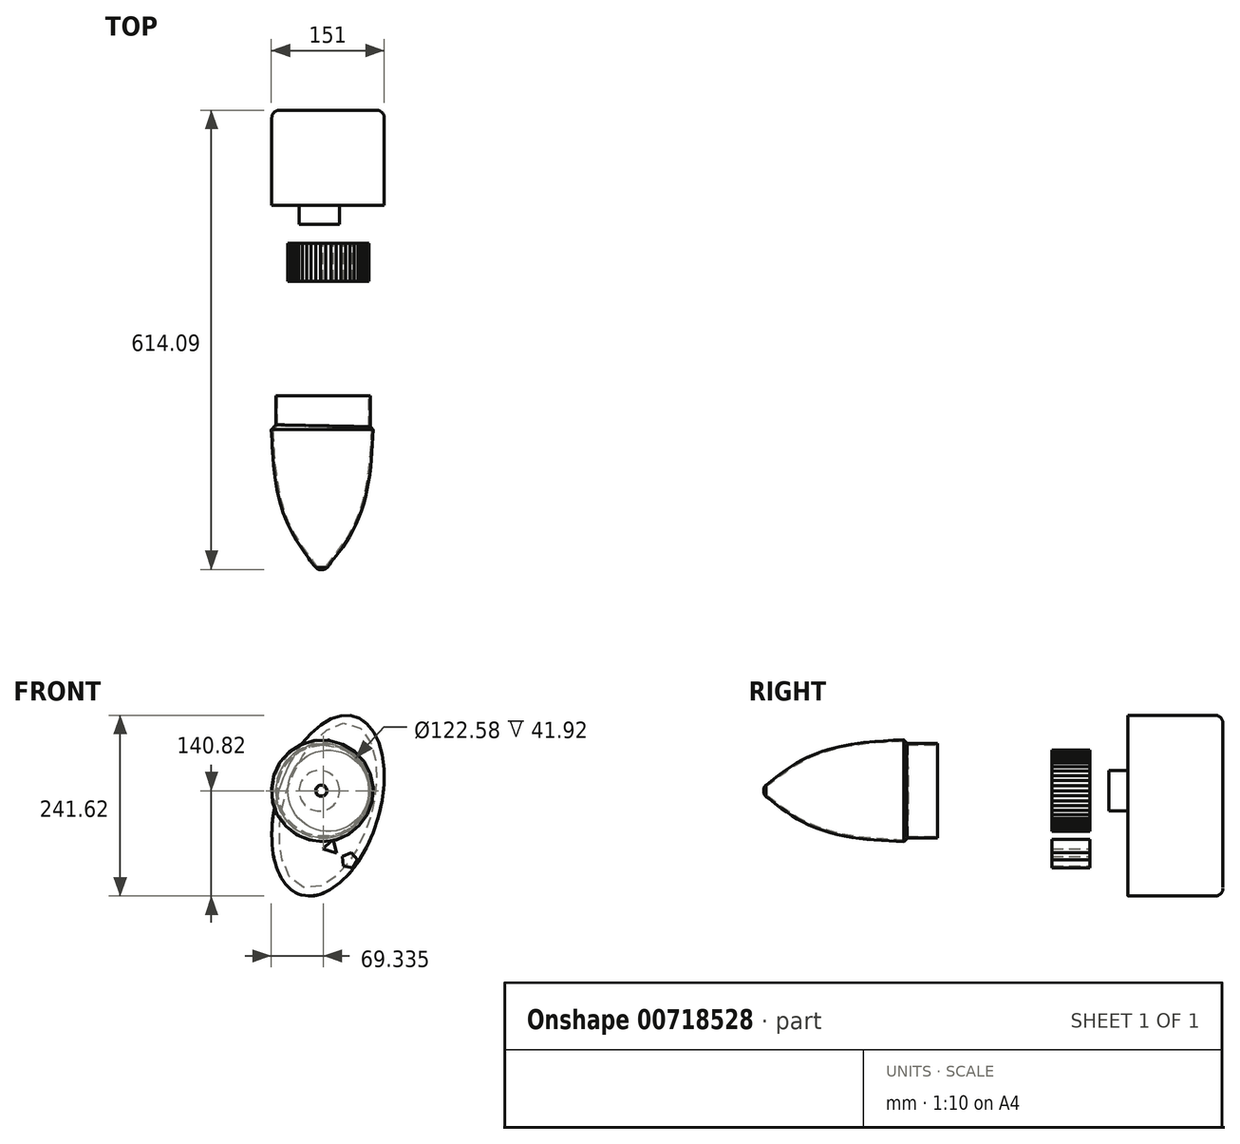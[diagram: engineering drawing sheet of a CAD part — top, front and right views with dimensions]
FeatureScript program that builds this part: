
annotation { "Feature Type Name" : "Feature", "Feature Type Description" : "" }
export const myFeature = defineFeature(function(context is Context, id is Id, definition is map)
    precondition{}
    {
        {
            var Q0;
            Q0=qCreatedBy(makeId("Front.planeOp"),FACE);
            var sketch = newSketch(context, id + "F0", { "sketchPlane" : qUnion([Q0])});
            skEllipse(sketch, "E0", {"center": v(65.97, -20) * mm, "majorRadius": 68.93 * mm, "minorRadius": 124.5 * mm, "majorAxis": v(-0.96, 0.3)});
            skSolve(sketch);
        }
        {
            var Q0;
            Q0=makeQuery(id+"F0.imprint","IMPRINT",FACE,{"disambiguationData":[TD([[makeQuery(id+"F0.imprint","IMPRINT",EDGE,{"derivedFrom":sQuery(id+"F0.wireOp",EDGE,"E0")}),1.0]])]});
            extrude(context, id + "F1", {"entities" : qUnion([Q0]), "depth" : 127 * mm, "offsetDistance" : 25.4 * mm});
        }
        {
            var Q0;
            Q0=makeQuery(id+"F1.opExtrude","CAP_EDGE",EDGE,{"disambiguationData":[OSD([sQuery(id+"F0.wireOp",EDGE,"E0")])],"isStart":true});
            fillet(context, id + "F2", {"entities" : qUnion([Q0]), "radius" : 10.16 * mm, "tangentPropagation" : true, "allowEdgeOverflow" : false});
        }
        {
            var Q0;
            Q0=makeQuery(id+"F1.opExtrude","CAP_FACE",FACE,{"disambiguationData":[OSD([sQuery(id+"F0.wireOp",EDGE,"E0")])],"isStart":false});
            var sketch = newSketch(context, id + "F3", { "sketchPlane" : qUnion([Q0])});
            skCircle(sketch, "E1", {"center": v(54.3, 0) * mm, "radius": 27.07 * mm});
            skSolve(sketch);
        }
        {
            var Q0;
            Q0 = qSketchRegion(id + "F3", true);
            extrude(context, id + "F4", {"entities" : qUnion([Q0]), "operationType" : NewBodyOperationType.ADD, "depth" : 25.4 * mm, "offsetDistance" : 25.4 * mm});
        }
        {
            var Q0;
            Q0=makeQuery(id+"F1.opExtrude","CAP_FACE",FACE,{"disambiguationData":[OSD([sQuery(id+"F0.wireOp",EDGE,"E0")])],"isStart":false});
            cPlane(context, id + "F5", {"entities" : qUnion([Q0]), "cplaneType" : CPlaneType.OFFSET, "offset" : 50.8 * mm, "width" : 152.4 * mm, "height" : 152.4 * mm});
        }
        {
            var Q0;
            Q0=qCreatedBy(id+"F5.planeOp",FACE);
            var sketch = newSketch(context, id + "F6", { "sketchPlane" : qUnion([Q0])});
            skCircle(sketch, "E2.cCircle", {"center": v(-818.72, 4123.6) * mm, "radius": 253.69 * mm, "construction": true});
            skLineSegment(sketch, "E2.0", {"start": v(-616.57, 3970.34) * mm, "end": v(-850.38, 3871.9) * mm});
            skLineSegment(sketch, "E2.1", {"start": v(-850.38, 3871.9) * mm, "end": v(-1052.53, 4025.17) * mm});
            skLineSegment(sketch, "E2.2", {"start": v(-1052.53, 4025.17) * mm, "end": v(-1020.87, 4276.87) * mm});
            skLineSegment(sketch, "E2.3", {"start": v(-1020.87, 4276.87) * mm, "end": v(-787.06, 4375.3) * mm});
            skLineSegment(sketch, "E2.4", {"start": v(-787.06, 4375.3) * mm, "end": v(-584.91, 4222.04) * mm});
            skLineSegment(sketch, "E2.5", {"start": v(-584.91, 4222.04) * mm, "end": v(-616.57, 3970.34) * mm});
            skCircle(sketch, "E3.cCircle", {"center": v(66.43, 0) * mm, "radius": 54.26 * mm, "construction": true});
            skLineSegment(sketch, "E3.0", {"start": v(120.7, 0) * mm, "end": v(120.27, -6.8) * mm});
            skLineSegment(sketch, "E3.1", {"start": v(120.27, -6.8) * mm, "end": v(119, -13.5) * mm});
            skLineSegment(sketch, "E3.2", {"start": v(119, -13.5) * mm, "end": v(116.89, -19.98) * mm});
            skLineSegment(sketch, "E3.3", {"start": v(116.89, -19.98) * mm, "end": v(113.99, -26.14) * mm});
            skLineSegment(sketch, "E3.4", {"start": v(113.99, -26.14) * mm, "end": v(110.33, -31.9) * mm});
            skLineSegment(sketch, "E3.5", {"start": v(110.33, -31.9) * mm, "end": v(106, -37.15) * mm});
            skLineSegment(sketch, "E3.6", {"start": v(106, -37.15) * mm, "end": v(101.02, -41.81) * mm});
            skLineSegment(sketch, "E3.7", {"start": v(101.02, -41.81) * mm, "end": v(95.51, -45.82) * mm});
            skLineSegment(sketch, "E3.8", {"start": v(95.51, -45.82) * mm, "end": v(89.54, -49.1) * mm});
            skLineSegment(sketch, "E3.9", {"start": v(89.54, -49.1) * mm, "end": v(83.2, -51.6) * mm});
            skLineSegment(sketch, "E3.10", {"start": v(83.2, -51.6) * mm, "end": v(76.6, -53.3) * mm});
            skLineSegment(sketch, "E3.11", {"start": v(76.6, -53.3) * mm, "end": v(69.84, -54.16) * mm});
            skLineSegment(sketch, "E3.12", {"start": v(69.84, -54.16) * mm, "end": v(63.03, -54.16) * mm});
            skLineSegment(sketch, "E3.13", {"start": v(63.03, -54.16) * mm, "end": v(56.27, -53.3) * mm});
            skLineSegment(sketch, "E3.14", {"start": v(56.27, -53.3) * mm, "end": v(49.67, -51.6) * mm});
            skLineSegment(sketch, "E3.15", {"start": v(49.67, -51.6) * mm, "end": v(43.33, -49.1) * mm});
            skLineSegment(sketch, "E3.16", {"start": v(43.33, -49.1) * mm, "end": v(37.36, -45.82) * mm});
            skLineSegment(sketch, "E3.17", {"start": v(37.36, -45.82) * mm, "end": v(31.84, -41.81) * mm});
            skLineSegment(sketch, "E3.18", {"start": v(31.84, -41.81) * mm, "end": v(26.88, -37.15) * mm});
            skLineSegment(sketch, "E3.19", {"start": v(26.88, -37.15) * mm, "end": v(22.53, -31.9) * mm});
            skLineSegment(sketch, "E3.20", {"start": v(22.53, -31.9) * mm, "end": v(18.88, -26.14) * mm});
            skLineSegment(sketch, "E3.21", {"start": v(18.88, -26.14) * mm, "end": v(15.98, -19.98) * mm});
            skLineSegment(sketch, "E3.22", {"start": v(15.98, -19.98) * mm, "end": v(13.87, -13.5) * mm});
            skLineSegment(sketch, "E3.23", {"start": v(13.87, -13.5) * mm, "end": v(12.6, -6.8) * mm});
            skLineSegment(sketch, "E3.24", {"start": v(12.6, -6.8) * mm, "end": v(12.17, 0) * mm});
            skLineSegment(sketch, "E3.25", {"start": v(12.17, 0) * mm, "end": v(12.6, 6.8) * mm});
            skLineSegment(sketch, "E3.26", {"start": v(12.6, 6.8) * mm, "end": v(13.87, 13.5) * mm});
            skLineSegment(sketch, "E3.27", {"start": v(13.87, 13.5) * mm, "end": v(15.98, 19.98) * mm});
            skLineSegment(sketch, "E3.28", {"start": v(15.98, 19.98) * mm, "end": v(18.88, 26.14) * mm});
            skLineSegment(sketch, "E3.29", {"start": v(18.88, 26.14) * mm, "end": v(22.53, 31.9) * mm});
            skLineSegment(sketch, "E3.30", {"start": v(22.53, 31.9) * mm, "end": v(26.88, 37.15) * mm});
            skLineSegment(sketch, "E3.31", {"start": v(26.88, 37.15) * mm, "end": v(31.84, 41.81) * mm});
            skLineSegment(sketch, "E3.32", {"start": v(31.84, 41.81) * mm, "end": v(37.36, 45.82) * mm});
            skLineSegment(sketch, "E3.33", {"start": v(37.36, 45.82) * mm, "end": v(43.33, 49.1) * mm});
            skLineSegment(sketch, "E3.34", {"start": v(43.33, 49.1) * mm, "end": v(49.67, 51.6) * mm});
            skLineSegment(sketch, "E3.35", {"start": v(49.67, 51.6) * mm, "end": v(56.27, 53.3) * mm});
            skLineSegment(sketch, "E3.36", {"start": v(56.27, 53.3) * mm, "end": v(63.03, 54.16) * mm});
            skLineSegment(sketch, "E3.37", {"start": v(63.03, 54.16) * mm, "end": v(69.84, 54.16) * mm});
            skLineSegment(sketch, "E3.38", {"start": v(69.84, 54.16) * mm, "end": v(76.6, 53.3) * mm});
            skLineSegment(sketch, "E3.39", {"start": v(76.6, 53.3) * mm, "end": v(83.2, 51.6) * mm});
            skLineSegment(sketch, "E3.40", {"start": v(83.2, 51.6) * mm, "end": v(89.54, 49.1) * mm});
            skLineSegment(sketch, "E3.41", {"start": v(89.54, 49.1) * mm, "end": v(95.51, 45.82) * mm});
            skLineSegment(sketch, "E3.42", {"start": v(95.51, 45.82) * mm, "end": v(101.02, 41.81) * mm});
            skLineSegment(sketch, "E3.43", {"start": v(101.02, 41.81) * mm, "end": v(106, 37.15) * mm});
            skLineSegment(sketch, "E3.44", {"start": v(106, 37.15) * mm, "end": v(110.33, 31.9) * mm});
            skLineSegment(sketch, "E3.45", {"start": v(110.33, 31.9) * mm, "end": v(113.99, 26.14) * mm});
            skLineSegment(sketch, "E3.46", {"start": v(113.99, 26.14) * mm, "end": v(116.89, 19.98) * mm});
            skLineSegment(sketch, "E3.47", {"start": v(116.89, 19.98) * mm, "end": v(119, 13.5) * mm});
            skLineSegment(sketch, "E3.48", {"start": v(119, 13.5) * mm, "end": v(120.27, 6.8) * mm});
            skLineSegment(sketch, "E3.49", {"start": v(120.27, 6.8) * mm, "end": v(120.7, 0) * mm});
            skCircle(sketch, "E4.cCircle", {"center": v(69.84, -75.35) * mm, "radius": 11 * mm, "construction": true});
            skLineSegment(sketch, "E4.0", {"start": v(77.49, -83.26) * mm, "end": v(59.16, -78.01) * mm});
            skLineSegment(sketch, "E4.1", {"start": v(59.16, -78.01) * mm, "end": v(72.87, -64.77) * mm});
            skLineSegment(sketch, "E4.2", {"start": v(72.87, -64.77) * mm, "end": v(77.49, -83.26) * mm});
            skCircle(sketch, "E5.cCircle", {"center": v(94.71, -93.16) * mm, "radius": 10.8 * mm, "construction": true});
            skLineSegment(sketch, "E5.0", {"start": v(99.01, -103.06) * mm, "end": v(86.63, -100.3) * mm});
            skLineSegment(sketch, "E5.1", {"start": v(86.63, -100.3) * mm, "end": v(85.42, -87.68) * mm});
            skLineSegment(sketch, "E5.2", {"start": v(85.42, -87.68) * mm, "end": v(97.05, -82.63) * mm});
            skLineSegment(sketch, "E5.3", {"start": v(97.05, -82.63) * mm, "end": v(105.46, -92.13) * mm});
            skLineSegment(sketch, "E5.4", {"start": v(105.46, -92.13) * mm, "end": v(99.01, -103.06) * mm});
            skSolve(sketch);
        }
        {
            var Q0;
            Q0=makeQuery(id+"F6.imprint","IMPRINT",FACE,{"disambiguationData":[TD([[makeQuery(id+"F6.imprint","IMPRINT",EDGE,{"derivedFrom":sQuery(id+"F6.wireOp",EDGE,"E3.0")}),-1.0]])]});
            var Q1;
            Q1=makeQuery(id+"F6.imprint","IMPRINT",FACE,{"disambiguationData":[TD([[makeQuery(id+"F6.imprint","IMPRINT",EDGE,{"derivedFrom":sQuery(id+"F6.wireOp",EDGE,"E5.0")}),-1.0]])]});
            var Q2;
            Q2=makeQuery(id+"F6.imprint","IMPRINT",FACE,{"disambiguationData":[TD([[makeQuery(id+"F6.imprint","IMPRINT",EDGE,{"derivedFrom":sQuery(id+"F6.wireOp",EDGE,"E4.0")}),-1.0]])]});
            extrude(context, id + "F7", {"entities" : qUnion([Q0, Q1, Q2]), "depth" : 50.8 * mm, "offsetDistance" : 25.4 * mm});
        }
        {
            var Q0;
            Q0=makeQuery(id+"F7.opExtrude","CAP_FACE",FACE,{"disambiguationData":[OSD([sQuery(id+"F6.wireOp",EDGE,"E3.0"),sQuery(id+"F6.wireOp",EDGE,"E3.1"),sQuery(id+"F6.wireOp",EDGE,"E3.2"),sQuery(id+"F6.wireOp",EDGE,"E3.3"),sQuery(id+"F6.wireOp",EDGE,"E3.4"),sQuery(id+"F6.wireOp",EDGE,"E3.5"),sQuery(id+"F6.wireOp",EDGE,"E3.6"),sQuery(id+"F6.wireOp",EDGE,"E3.7"),sQuery(id+"F6.wireOp",EDGE,"E3.8"),sQuery(id+"F6.wireOp",EDGE,"E3.9"),sQuery(id+"F6.wireOp",EDGE,"E3.10"),sQuery(id+"F6.wireOp",EDGE,"E3.11"),sQuery(id+"F6.wireOp",EDGE,"E3.12"),sQuery(id+"F6.wireOp",EDGE,"E3.13"),sQuery(id+"F6.wireOp",EDGE,"E3.14"),sQuery(id+"F6.wireOp",EDGE,"E3.15"),sQuery(id+"F6.wireOp",EDGE,"E3.16"),sQuery(id+"F6.wireOp",EDGE,"E3.17"),sQuery(id+"F6.wireOp",EDGE,"E3.18"),sQuery(id+"F6.wireOp",EDGE,"E3.19"),sQuery(id+"F6.wireOp",EDGE,"E3.20"),sQuery(id+"F6.wireOp",EDGE,"E3.21"),sQuery(id+"F6.wireOp",EDGE,"E3.22"),sQuery(id+"F6.wireOp",EDGE,"E3.23"),sQuery(id+"F6.wireOp",EDGE,"E3.24"),sQuery(id+"F6.wireOp",EDGE,"E3.25"),sQuery(id+"F6.wireOp",EDGE,"E3.26"),sQuery(id+"F6.wireOp",EDGE,"E3.27"),sQuery(id+"F6.wireOp",EDGE,"E3.28"),sQuery(id+"F6.wireOp",EDGE,"E3.29"),sQuery(id+"F6.wireOp",EDGE,"E3.30"),sQuery(id+"F6.wireOp",EDGE,"E3.31"),sQuery(id+"F6.wireOp",EDGE,"E3.32"),sQuery(id+"F6.wireOp",EDGE,"E3.33"),sQuery(id+"F6.wireOp",EDGE,"E3.34"),sQuery(id+"F6.wireOp",EDGE,"E3.35"),sQuery(id+"F6.wireOp",EDGE,"E3.36"),sQuery(id+"F6.wireOp",EDGE,"E3.37"),sQuery(id+"F6.wireOp",EDGE,"E3.38"),sQuery(id+"F6.wireOp",EDGE,"E3.39"),sQuery(id+"F6.wireOp",EDGE,"E3.40"),sQuery(id+"F6.wireOp",EDGE,"E3.41"),sQuery(id+"F6.wireOp",EDGE,"E3.42"),sQuery(id+"F6.wireOp",EDGE,"E3.43"),sQuery(id+"F6.wireOp",EDGE,"E3.44"),sQuery(id+"F6.wireOp",EDGE,"E3.45"),sQuery(id+"F6.wireOp",EDGE,"E3.46"),sQuery(id+"F6.wireOp",EDGE,"E3.47"),sQuery(id+"F6.wireOp",EDGE,"E3.48"),sQuery(id+"F6.wireOp",EDGE,"E3.49")])],"isStart":false});
            cPlane(context, id + "F8", {"entities" : qUnion([Q0]), "cplaneType" : CPlaneType.OFFSET, "offset" : 103.5 * mm, "width" : 150 * mm, "height" : 150 * mm});
        }
        {
            var Q0;
            Q0=qCreatedBy(id+"F8.planeOp",FACE);
            var sketch = newSketch(context, id + "F9", { "sketchPlane" : qUnion([Q0])});
            skCircle(sketch, "E6", {"center": v(59.42, 0) * mm, "radius": 59.03 * mm});
            skSolve(sketch);
        }
        {
            var Q0;
            Q0=makeQuery(id+"F9.imprint","IMPRINT",FACE,{"disambiguationData":[TD([[makeQuery(id+"F9.imprint","IMPRINT",EDGE,{"derivedFrom":sQuery(id+"F9.wireOp",EDGE,"E6")}),1.0]])]});
            cPlane(context, id + "F10", {"entities" : qUnion([Q0]), "cplaneType" : CPlaneType.OFFSET, "offset" : 50 * mm, "width" : 150 * mm, "height" : 150 * mm});
        }
        {
            var Q0;
            Q0=qCreatedBy(id+"F10.planeOp",FACE);
            var sketch = newSketch(context, id + "F11", { "sketchPlane" : qUnion([Q0])});
            skCircle(sketch, "E7", {"center": v(59.52, 0) * mm, "radius": 61.29 * mm});
            skSolve(sketch);
        }
        {
            var Q0;
            Q0=makeQuery(id+"F11.imprint","IMPRINT",FACE,{"disambiguationData":[TD([[makeQuery(id+"F11.imprint","IMPRINT",EDGE,{"derivedFrom":sQuery(id+"F11.wireOp",EDGE,"E7")}),1.0]])]});
            cPlane(context, id + "F12", {"entities" : qUnion([Q0]), "cplaneType" : CPlaneType.OFFSET, "offset" : 30 * mm, "width" : 150 * mm, "height" : 150 * mm});
        }
        {
            var Q0;
            Q0=qCreatedBy(id+"F12.planeOp",FACE);
            var sketch = newSketch(context, id + "F13", { "sketchPlane" : qUnion([Q0])});
            skCircle(sketch, "E8", {"center": v(58.32, 0) * mm, "radius": 66.66 * mm});
            skSolve(sketch);
        }
        {
            var Q0;
            Q0=makeQuery(id+"F13.imprint","IMPRINT",FACE,{"disambiguationData":[TD([[makeQuery(id+"F13.imprint","IMPRINT",EDGE,{"derivedFrom":sQuery(id+"F13.wireOp",EDGE,"E8")}),1.0]])]});
            cPlane(context, id + "F14", {"entities" : qUnion([Q0]), "cplaneType" : CPlaneType.OFFSET, "offset" : 200 * mm, "width" : 150 * mm, "height" : 150 * mm});
        }
        {
            var Q0;
            Q0=qCreatedBy(id+"F14.planeOp",FACE);
            var sketch = newSketch(context, id + "F15", { "sketchPlane" : qUnion([Q0])});
            skCircle(sketch, "E9", {"center": v(57.1, 0) * mm, "radius": 4.48 * mm});
            skSolve(sketch);
        }
        {
            var Q0;
            Q0=sQuery(id+"F9.wireOp",EDGE,"E6");
            extrude(context, id + "F16", {"bodyType" : ToolBodyType.SURFACE, "surfaceEntities" : qUnion([Q0]), "depth" : 50 * mm, "offsetDistance" : 25 * mm});
        }
        {
            var Q0;
            Q0=makeQuery(id+"F11.imprint","IMPRINT",FACE,{"disambiguationData":[TD([[makeQuery(id+"F11.imprint","IMPRINT",EDGE,{"derivedFrom":sQuery(id+"F11.wireOp",EDGE,"E7")}),1.0]])]});
            extrude(context, id + "F17", {"entities" : qUnion([Q0]), "depth" : 30 * mm, "offsetDistance" : 25 * mm});
        }
        {
            var Q0;
            Q0=makeQuery(id+"F13.imprint","IMPRINT",FACE,{"disambiguationData":[TD([[makeQuery(id+"F13.imprint","IMPRINT",EDGE,{"derivedFrom":sQuery(id+"F13.wireOp",EDGE,"E8")}),1.0]])]});
            cPlane(context, id + "F18", {"entities" : qUnion([Q0]), "cplaneType" : CPlaneType.OFFSET, "offset" : 50 * mm, "width" : 150 * mm, "height" : 150 * mm});
        }
        {
            var Q0;
            Q0=qCreatedBy(id+"F18.planeOp",FACE);
            cPlane(context, id + "F19", {"entities" : qUnion([Q0]), "cplaneType" : CPlaneType.OFFSET, "offset" : 100 * mm, "width" : 150 * mm, "height" : 150 * mm});
        }
        {
            var Q0;
            Q0=qCreatedBy(id+"F19.planeOp",FACE);
            var sketch = newSketch(context, id + "F20", { "sketchPlane" : qUnion([Q0])});
            skCircle(sketch, "E10", {"center": v(57.7, 0) * mm, "radius": 39.32 * mm});
            skSolve(sketch);
        }
        {
            var Q1;
            Q1 = qSketchRegion(id + "F15", true);
            var Q2;
            Q2 = qSketchRegion(id + "F20", true);
            var Q3;
            Q3 = qSketchRegion(id + "F13", true);
            loft(context, id + "F21", {"operationType" : NewBodyOperationType.ADD, "sheetProfilesArray" : [{ "sheetProfileEntities" : qUnion([Q1]) }, { "sheetProfileEntities" : qUnion([Q2]) }, { "sheetProfileEntities" : qUnion([Q3]) }]});
        }
        {
            var Q0;
            Q0=makeQuery(id+"F21.opLoft","MID_CAP_EDGE",EDGE,{"disambiguationData":[OSD([sQuery(id+"F15.wireOp",EDGE,"E9")])],"capPos":0.0});
            fillet(context, id + "F22", {"entities" : qUnion([Q0]), "radius" : 5 * mm, "tangentPropagation" : true, "allowEdgeOverflow" : false});
        }
        {
            var Q0;
            Q0=makeQuery(id+"F21.opLoft","MID_CAP_EDGE",EDGE,{"disambiguationData":[OSD([sQuery(id+"F13.wireOp",EDGE,"E8")])],"capPos":2.0});
            chamfer(context, id + "F23", {"entities" : qUnion([Q0]), "width" : 15 * mm, "tangentPropagation" : true});
        }
        {
            var Q0;
            Q0=makeQuery(id+"F17.opExtrude","CAP_FACE",FACE,{"disambiguationData":[OSD([sQuery(id+"F11.wireOp",EDGE,"E7")])],"isStart":true});
            var Q1;
            Q1=makeQuery(id+"F17.opExtrude","SWEPT_BODY",BODY,{"disambiguationData":[OSD([sQuery(id+"F11.wireOp",EDGE,"E7")])]});
            shell(context, id + "F24", {"entities" : qUnion([Q0]), "parts" : qUnion([Q1]), "thickness" : 2 * mm, "oppositeDirection" : true});
        }
    });
